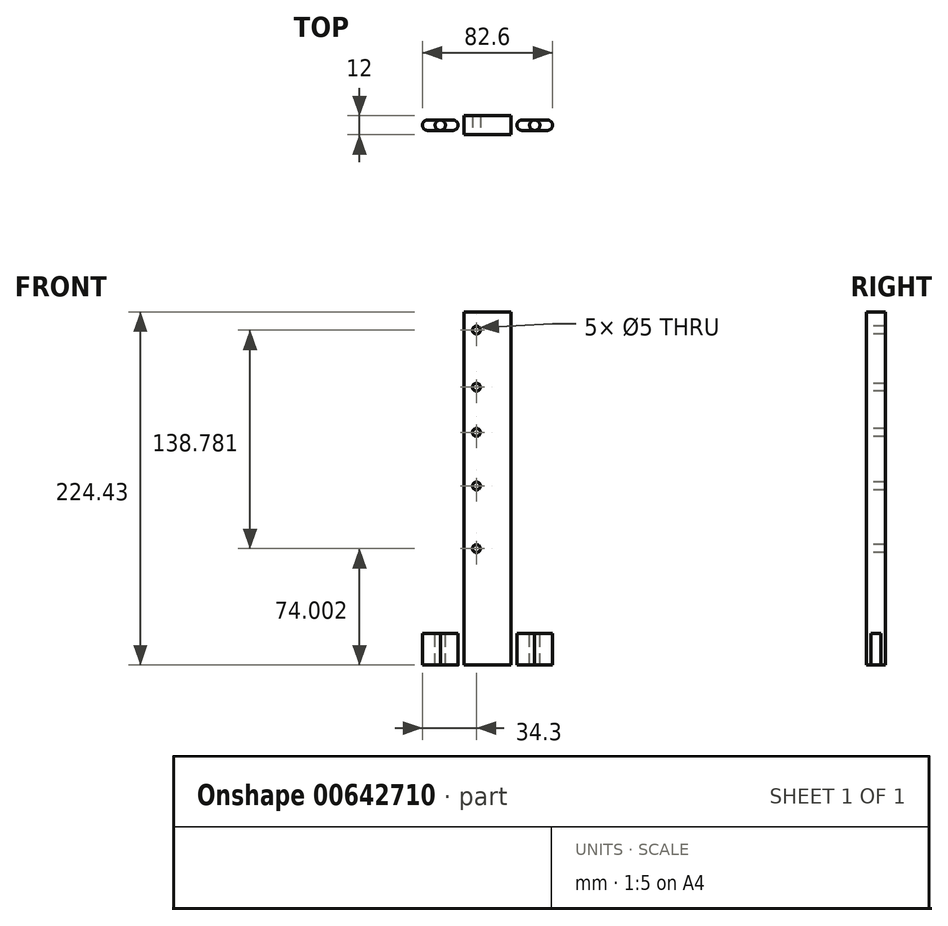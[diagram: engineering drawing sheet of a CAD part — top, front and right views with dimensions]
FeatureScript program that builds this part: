
annotation { "Feature Type Name" : "Feature", "Feature Type Description" : "" }
export const myFeature = defineFeature(function(context is Context, id is Id, definition is map)
    precondition{}
    {
        {
            var Q0;
            Q0=qCreatedBy(makeId("Front.planeOp"),FACE);
            var sketch = newSketch(context, id + "F0", { "sketchPlane" : qUnion([Q0])});
            skLineSegment(sketch, "E0", {"start": v(0, 0) * mm, "end": v(0, 20) * mm});
            skLineSegment(sketch, "E1", {"start": v(0, 20) * mm, "end": v(30, 20) * mm});
            skLineSegment(sketch, "E2", {"start": v(30, 20) * mm, "end": v(30, 224.43) * mm});
            skLineSegment(sketch, "E3", {"start": v(30, 224.43) * mm, "end": v(60, 224.43) * mm});
            skLineSegment(sketch, "E4", {"start": v(60, 224.43) * mm, "end": v(60, 20) * mm});
            skLineSegment(sketch, "E5", {"start": v(60, 20) * mm, "end": v(90, 20) * mm});
            skLineSegment(sketch, "E6", {"start": v(90, 20) * mm, "end": v(90, 0) * mm});
            skLineSegment(sketch, "E7", {"start": v(0, 0) * mm, "end": v(90, 0) * mm});
            skSolve(sketch);
        }
        {
            var Q0;
            Q0=makeQuery(id+"F0.imprint","IMPRINT",FACE,{"disambiguationData":[TD([[makeQuery(id+"F0.imprint","IMPRINT",EDGE,{"derivedFrom":sQuery(id+"F0.wireOp",EDGE,"E0")}),-1.0]])]});
            extrude(context, id + "F1", {"entities" : qUnion([Q0]), "depth" : 12 * mm, "offsetDistance" : 25 * mm});
        }
        {
            var Q0;
            Q0=makeQuery(id+"F1.opExtrude","CAP_FACE",FACE,{"disambiguationData":[OSD([sQuery(id+"F0.wireOp",EDGE,"E0"),sQuery(id+"F0.wireOp",EDGE,"E1"),sQuery(id+"F0.wireOp",EDGE,"E2"),sQuery(id+"F0.wireOp",EDGE,"E3"),sQuery(id+"F0.wireOp",EDGE,"E4"),sQuery(id+"F0.wireOp",EDGE,"E5"),sQuery(id+"F0.wireOp",EDGE,"E6"),sQuery(id+"F0.wireOp",EDGE,"E7")])],"isStart":false});
            var sketch = newSketch(context, id + "F2", { "sketchPlane" : qUnion([Q0])});
            skLineSegment(sketch, "E8", {"start": v(38, 224.43) * mm, "end": v(38, 25.97) * mm, "construction": true});
            skPoint(sketch, "E9", {"position": v(38, 212.78) * mm});
            skPoint(sketch, "E10", {"position": v(38, 176.52) * mm});
            skPoint(sketch, "E11", {"position": v(38, 147.86) * mm});
            skPoint(sketch, "E12", {"position": v(38, 113.82) * mm});
            skPoint(sketch, "E13", {"position": v(38, 74) * mm});
            skSolve(sketch);
        }
        {
            var Q0;
            Q0=sQuery(id+"F2.wireOp",VERTEX,"E9");
            var Q1;
            Q1=sQuery(id+"F2.wireOp",VERTEX,"E10");
            var Q2;
            Q2=sQuery(id+"F2.wireOp",VERTEX,"E11");
            var Q3;
            Q3=sQuery(id+"F2.wireOp",VERTEX,"E12");
            var Q4;
            Q4=sQuery(id+"F2.wireOp",VERTEX,"E13");
            var Q5;
            Q5=makeQuery(id+"F1.opExtrude","SWEPT_BODY",BODY,{"disambiguationData":[OSD([sQuery(id+"F0.wireOp",EDGE,"E0"),sQuery(id+"F0.wireOp",EDGE,"E1"),sQuery(id+"F0.wireOp",EDGE,"E2"),sQuery(id+"F0.wireOp",EDGE,"E3"),sQuery(id+"F0.wireOp",EDGE,"E4"),sQuery(id+"F0.wireOp",EDGE,"E5"),sQuery(id+"F0.wireOp",EDGE,"E6"),sQuery(id+"F0.wireOp",EDGE,"E7")])]});
            hole(context, id + "F3", {"style" : HoleStyle.SIMPLE, "endStyle" : HoleEndStyle.THROUGH, "holeDiameter" : 5 * mm, "majorDiameter" : 5 * mm, "isTappedThrough" : true, "tappedDepth" : 12 * mm, "tapClearance" : 3, "locations" : qUnion([Q0, Q1, Q2, Q3, Q4]), "scope" : qUnion([Q5])});
        }
        {
            var Q0;
            Q0=makeQuery(id+"F1.opExtrude","SWEPT_FACE",FACE,{"disambiguationData":[OSD([sQuery(id+"F0.wireOp",EDGE,"E1")])]});
            var sketch = newSketch(context, id + "F4", { "sketchPlane" : qUnion([Q0])});
            skLineSegment(sketch, "E14", {"start": v(15, -6) * mm, "end": v(7, -6) * mm});
            skPoint(sketch, "E14.startSnap0", {"position": v(0, -6) * mm});
            skPoint(sketch, "E14.startSnap1", {"position": v(15, 0) * mm});
            skLineSegment(sketch, "E15", {"start": v(15, -6) * mm, "end": v(23, -6) * mm});
            skArc(sketch, "E16.0.startCap", {"start": v(15, -2.7) * mm, "mid": v(18.3, -6) * mm, "end": v(15, -9.3) * mm});
            skArc(sketch, "E16.0.endCap", {"start": v(7, -9.3) * mm, "mid": v(3.7, -6) * mm, "end": v(7, -2.7) * mm});
            skLineSegment(sketch, "E16.0.left", {"start": v(15, -9.3) * mm, "end": v(7, -9.3) * mm});
            skLineSegment(sketch, "E16.0.right", {"start": v(15, -2.7) * mm, "end": v(7, -2.7) * mm});
            skArc(sketch, "E16.1.startCap", {"start": v(15, -9.3) * mm, "mid": v(11.7, -6) * mm, "end": v(15, -2.7) * mm});
            skArc(sketch, "E16.1.endCap", {"start": v(23, -2.7) * mm, "mid": v(26.3, -6) * mm, "end": v(23, -9.3) * mm});
            skLineSegment(sketch, "E16.1.left", {"start": v(15, -2.7) * mm, "end": v(23, -2.7) * mm});
            skLineSegment(sketch, "E16.1.right", {"start": v(15, -9.3) * mm, "end": v(23, -9.3) * mm});
            skSolve(sketch);
        }
        {
            var Q0;
            Q0=makeQuery(id+"F1.opExtrude","SWEPT_FACE",FACE,{"disambiguationData":[OSD([sQuery(id+"F0.wireOp",EDGE,"E5")])]});
            var sketch = newSketch(context, id + "F5", { "sketchPlane" : qUnion([Q0])});
            skLineSegment(sketch, "E17", {"start": v(75, -6) * mm, "end": v(67, -6) * mm});
            skPoint(sketch, "E17.startSnap0", {"position": v(75, 0) * mm});
            skPoint(sketch, "E17.startSnap1", {"position": v(90, -6) * mm});
            skLineSegment(sketch, "E18", {"start": v(75, -6) * mm, "end": v(83, -6) * mm});
            skArc(sketch, "E19.0.startCap", {"start": v(75, -2.7) * mm, "mid": v(78.3, -6) * mm, "end": v(75, -9.3) * mm});
            skArc(sketch, "E19.0.endCap", {"start": v(67, -9.3) * mm, "mid": v(63.7, -6) * mm, "end": v(67, -2.7) * mm});
            skLineSegment(sketch, "E19.0.left", {"start": v(75, -9.3) * mm, "end": v(67, -9.3) * mm});
            skLineSegment(sketch, "E19.0.right", {"start": v(75, -2.7) * mm, "end": v(67, -2.7) * mm});
            skArc(sketch, "E19.1.startCap", {"start": v(75, -9.3) * mm, "mid": v(71.7, -6) * mm, "end": v(75, -2.7) * mm});
            skArc(sketch, "E19.1.endCap", {"start": v(83, -2.7) * mm, "mid": v(86.3, -6) * mm, "end": v(83, -9.3) * mm});
            skLineSegment(sketch, "E19.1.left", {"start": v(75, -2.7) * mm, "end": v(83, -2.7) * mm});
            skLineSegment(sketch, "E19.1.right", {"start": v(75, -9.3) * mm, "end": v(83, -9.3) * mm});
            skSolve(sketch);
        }
        {
            var Q0;
            Q0=makeQuery(id+"F4.imprint","IMPRINT",FACE,{"disambiguationData":[TD([[makeQuery(id+"F4.imprint","IMPRINT",EDGE,{"derivedFrom":sQuery(id+"F4.wireOp",EDGE,"E16.0.endCap")}),-1.0]])]});
            var Q1;
            {var subQ0=sQuery(id+"F4.wireOp",EDGE,"E15");var subQ1=sQuery(id+"F4.wireOp",EDGE,"E14");var subQ2=makeQuery(id+"F4.imprint","INTERSECT",VERTEX,{"derivedFrom":[subQ1,subQ0]});Q1=makeQuery(id+"F4.imprint","IMPRINT",FACE,{"disambiguationData":[TD([[makeQuery(id+"F4.imprint","IMPRINT",EDGE,{"disambiguationData":[TD([[subQ2,-1.0]])],"derivedFrom":subQ1}),1.0]])]});}
            var Q2;
            Q2=makeQuery(id+"F4.imprint","IMPRINT",FACE,{"disambiguationData":[TD([[makeQuery(id+"F4.imprint","IMPRINT",EDGE,{"derivedFrom":sQuery(id+"F4.wireOp",EDGE,"E16.1.endCap")}),-1.0]])]});
            var Q3;
            {var subQ0=sQuery(id+"F4.wireOp",EDGE,"E15");var subQ1=sQuery(id+"F4.wireOp",EDGE,"E14");var subQ2=makeQuery(id+"F4.imprint","INTERSECT",VERTEX,{"derivedFrom":[subQ1,subQ0]});Q3=makeQuery(id+"F4.imprint","IMPRINT",FACE,{"disambiguationData":[TD([[makeQuery(id+"F4.imprint","IMPRINT",EDGE,{"disambiguationData":[TD([[subQ2,-1.0]])],"derivedFrom":subQ1}),-1.0]])]});}
            var Q4;
            Q4=makeQuery(id+"F5.imprint","IMPRINT",FACE,{"disambiguationData":[TD([[makeQuery(id+"F5.imprint","IMPRINT",EDGE,{"derivedFrom":sQuery(id+"F5.wireOp",EDGE,"E19.0.endCap")}),-1.0]])]});
            var Q5;
            {var subQ0=sQuery(id+"F5.wireOp",EDGE,"E18");var subQ1=sQuery(id+"F5.wireOp",EDGE,"E17");var subQ2=makeQuery(id+"F5.imprint","INTERSECT",VERTEX,{"derivedFrom":[subQ1,subQ0]});Q5=makeQuery(id+"F5.imprint","IMPRINT",FACE,{"disambiguationData":[TD([[makeQuery(id+"F5.imprint","IMPRINT",EDGE,{"disambiguationData":[TD([[subQ2,-1.0]])],"derivedFrom":subQ1}),1.0]])]});}
            var Q6;
            {var subQ0=sQuery(id+"F5.wireOp",EDGE,"E18");var subQ1=sQuery(id+"F5.wireOp",EDGE,"E17");var subQ2=makeQuery(id+"F5.imprint","INTERSECT",VERTEX,{"derivedFrom":[subQ1,subQ0]});Q6=makeQuery(id+"F5.imprint","IMPRINT",FACE,{"disambiguationData":[TD([[makeQuery(id+"F5.imprint","IMPRINT",EDGE,{"disambiguationData":[TD([[subQ2,-1.0]])],"derivedFrom":subQ1}),-1.0]])]});}
            var Q7;
            Q7=makeQuery(id+"F5.imprint","IMPRINT",FACE,{"disambiguationData":[TD([[makeQuery(id+"F5.imprint","IMPRINT",EDGE,{"derivedFrom":sQuery(id+"F5.wireOp",EDGE,"E19.1.endCap")}),-1.0]])]});
            extrude(context, id + "F6", {"entities" : qUnion([Q0, Q1, Q2, Q3, Q4, Q5, Q6, Q7]), "operationType" : NewBodyOperationType.REMOVE, "endBound" : BoundingType.THROUGH_ALL, "oppositeDirection" : true, "depth" : 25 * mm, "offsetDistance" : 25 * mm});
        }
    });
